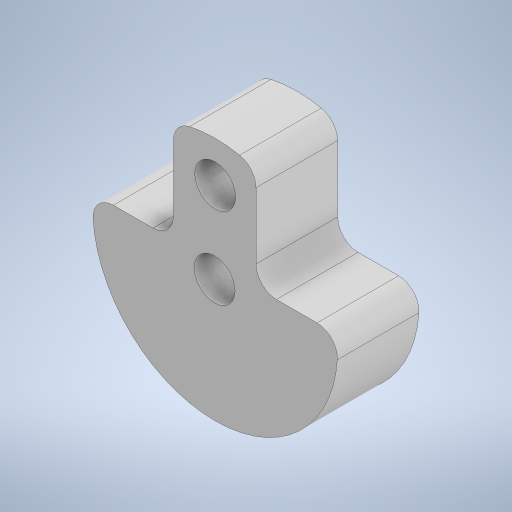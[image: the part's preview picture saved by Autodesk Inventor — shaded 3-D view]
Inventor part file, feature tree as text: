
AUTODESK INVENTOR PART (.ipt)
format: ipt  version: 2023 (Build 270158000, 158)  size: 250,880 bytes
history: native  units: in
note: dims shown in document units (in); Inventor stores cm internally (conversion verified against a paired STEP export)
features: extrude x1, sketch x1
ambient origin geometry x8: Origin, YZ Plane, XZ Plane, XY Plane, X Axis, Y Axis, Z Axis, Center Point
bodies: Solid1 (feature_tree)
feature tree (2):
  extrude  "Extrusion1"  Depth=0.5in
  sketch  "Sketch1"  dims[d2=1.5in d3=0.25in d6=0.25in d7=0.5in d8=0.0in d11=0.625in d12=0.125in d10=0.5in d13=0.0344in]
